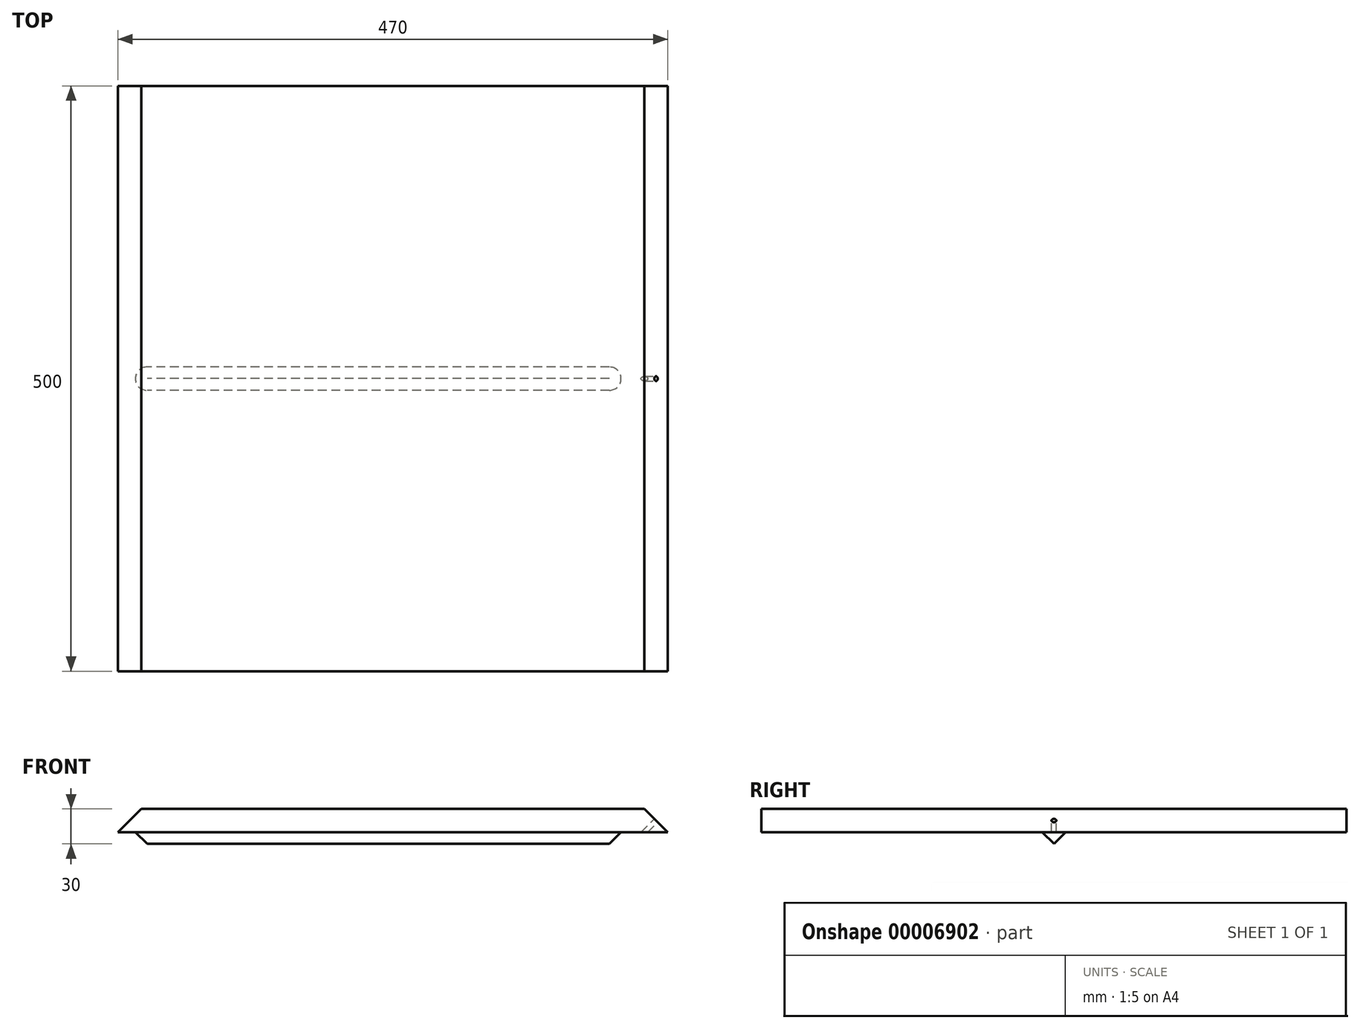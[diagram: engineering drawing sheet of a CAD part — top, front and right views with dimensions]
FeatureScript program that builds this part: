
annotation { "Feature Type Name" : "Feature", "Feature Type Description" : "" }
export const myFeature = defineFeature(function(context is Context, id is Id, definition is map)
    precondition{}
    {
        {
            var Q0;
            Q0=qCreatedBy(makeId("Top.planeOp"),FACE);
            var sketch = newSketch(context, id + "F0", { "sketchPlane" : qUnion([Q0])});
            skLineSegment(sketch, "E0.rect.bottom", {"start": v(242.5, -250) * mm, "end": v(-242.5, -250) * mm});
            skLineSegment(sketch, "E0.rect.top", {"start": v(242.5, 250) * mm, "end": v(-242.5, 250) * mm});
            skLineSegment(sketch, "E0.rect.left", {"start": v(242.5, -250) * mm, "end": v(242.5, 250) * mm});
            skLineSegment(sketch, "E0.rect.right", {"start": v(-242.5, -250) * mm, "end": v(-242.5, 250) * mm});
            skPoint(sketch, "E0.rect.middle", {"position": v(0, 0) * mm});
            skLineSegment(sketch, "E1", {"start": v(-242.5, 0) * mm, "end": v(242.5, 0) * mm, "construction": true});
            skSolve(sketch);
        }
        {
            var Q0;
            Q0=qSketchRegion(id+"F0",true);
            var Q1;
            Q1=makeQuery(id+"F0.imprint","IMPRINT",FACE,{"disambiguationData":[TD([[makeQuery(id+"F0.imprint","IMPRINT",EDGE,{"derivedFrom":sQuery(id+"F0.wireOp",EDGE,"E0.rect.bottom")}),-1.0]])]});
            extrude(context, id + "F1", {"entities" : qUnion([Q0, Q1]), "depth" : (30) * mm});
        }
        {
            var Q0;
            Q0=makeQuery(id+"F1.opExtrude","SWEPT_FACE",FACE,{"disambiguationData":[OSD([sQuery(id+"F0.wireOp",EDGE,"E0.rect.right")])]});
            var sketch = newSketch(context, id + "F2", { "sketchPlane" : qUnion([Q0])});
            skLineSegment(sketch, "E2", {"start": v(0, 0) * mm, "end": v(-10, 10) * mm});
            skLineSegment(sketch, "E3", {"start": v(0, 0) * mm, "end": v(10, 10) * mm});
            skLineSegment(sketch, "E4", {"start": v(-10, 10) * mm, "end": v(-250, 10) * mm});
            skLineSegment(sketch, "E5", {"start": v(10, 10) * mm, "end": v(250, 10) * mm});
            skSolve(sketch);
        }
        {
            var Q0;
            Q0=qSketchRegion(id+"F2",true);
            var Q1;
            {var subQ2=sQuery(id+"F2.wireOp",EDGE,"E2");Q1=makeQuery(id+"F2.imprint","IMPRINT",FACE,{"disambiguationData":[TD([[makeQuery(id+"F2.imprint","IMPRINT",EDGE,{"derivedFrom":subQ2}),1.0]])]});}
            var Q2;
            {var subQ2=sQuery(id+"F2.wireOp",EDGE,"E3");Q2=makeQuery(id+"F2.imprint","IMPRINT",FACE,{"disambiguationData":[TD([[makeQuery(id+"F2.imprint","IMPRINT",EDGE,{"derivedFrom":subQ2}),-1.0]])]});}
            extrude(context, id + "F3", {"entities" : qUnion([Q0, Q1, Q2]), "operationType" : NewBodyOperationType.REMOVE, "endBound" : BoundingType.THROUGH_ALL, "oppositeDirection" : true, "depth" : 25 * mm});
        }
        {
            var Q0;
            Q0=makeQuery(id+"F1.opExtrude","SWEPT_FACE",FACE,{"disambiguationData":[OSD([sQuery(id+"F0.wireOp",EDGE,"E0.rect.right")])]});
            var sketch = newSketch(context, id + "F4", { "sketchPlane" : qUnion([Q0])});
            skLineSegment(sketch, "E6", {"start": v(-10, 10) * mm, "end": v(10, 10) * mm});
            skSolve(sketch);
        }
        {
            var Q0;
            Q0=qSketchRegion(id+"F4",true);
            var Q1;
            Q1=makeQuery(id+"F4.imprint","IMPRINT",FACE,{"disambiguationData":[TD([[makeQuery(id+"F4.imprint","IMPRINT",EDGE,{"derivedFrom":sQuery(id+"F4.wireOp",EDGE,"E6")}),-1.0]])]});
            extrude(context, id + "F5", {"entities" : qUnion([Q0, Q1]), "operationType" : NewBodyOperationType.REMOVE, "oppositeDirection" : true, "depth" : 25 * mm});
        }
        {
            var Q0;
            Q0=makeQuery(id+"F5.boolean.opBoolean","COPY",FACE,{"derivedFrom":makeQuery(id+"F5.opExtrude","CAP_FACE",FACE,{"disambiguationData":[OSD([sQuery(id+"F2.wireOp",EDGE,"E2"),sQuery(id+"F2.wireOp",EDGE,"E3"),sQuery(id+"F4.wireOp",EDGE,"E6")])],"isStart":false})});
            var sketch = newSketch(context, id + "F6", { "sketchPlane" : qUnion([Q0])});
            skLineSegment(sketch, "E7", {"start": v(0, 0) * mm, "end": v(0, 10) * mm});
            skSolve(sketch);
        }
        {
            var Q0;
            {var subQ1=sQuery(id+"F6.wireOp",EDGE,"E7");Q0=makeQuery(id+"F6.imprint","IMPRINT",FACE,{"disambiguationData":[TD([[makeQuery(id+"F6.imprint","IMPRINT",EDGE,{"derivedFrom":subQ1}),1.0]])]});}
            var Q1;
            Q1=sQuery(id+"F6.wireOp",EDGE,"E7");
            revolve(context, id + "F7", {"operationType" : NewBodyOperationType.ADD, "entities" : qUnion([Q0]), "axis" : qUnion([Q1]), "revolveType" : RevolveType.FULL});
        }
        {
            var Q0;
            Q0=makeQuery(id+"F1.opExtrude","SWEPT_FACE",FACE,{"disambiguationData":[OSD([sQuery(id+"F0.wireOp",EDGE,"E0.rect.top")])]});
            var sketch = newSketch(context, id + "F8", { "sketchPlane" : qUnion([Q0])});
            skLineSegment(sketch, "E8", {"start": v(242.5, 10) * mm, "end": v(222.5, 30) * mm});
            skSolve(sketch);
        }
        {
            var Q0;
            Q0=qSketchRegion(id+"F8",true);
            var Q1;
            {var subQ2=sQuery(id+"F8.wireOp",EDGE,"E8");Q1=makeQuery(id+"F8.imprint","IMPRINT",FACE,{"disambiguationData":[TD([[makeQuery(id+"F8.imprint","IMPRINT",EDGE,{"derivedFrom":subQ2}),-1.0]])]});}
            extrude(context, id + "F9", {"entities" : qUnion([Q0, Q1]), "operationType" : NewBodyOperationType.REMOVE, "endBound" : BoundingType.THROUGH_ALL, "oppositeDirection" : true, "depth" : 25 * mm});
        }
        {
            var Q0;
            Q0=makeQuery(id+"F1.opExtrude","SWEPT_FACE",FACE,{"disambiguationData":[OSD([sQuery(id+"F0.wireOp",EDGE,"E0.rect.left")])]});
            extrude(context, id + "F10", {"entities" : qUnion([Q0]), "operationType" : NewBodyOperationType.REMOVE, "oppositeDirection" : true, "depth" : (15) * mm});
        }
        {
            var Q0;
            Q0=makeQuery(id+"F10.boolean.opBoolean","COPY",FACE,{"derivedFrom":makeQuery(id+"F10.opExtrude","CAP_FACE",FACE,{"disambiguationData":[OSD([sQuery(id+"F0.wireOp",EDGE,"E0.rect.left")])],"isStart":false})});
            var sketch = newSketch(context, id + "F11", { "sketchPlane" : qUnion([Q0])});
            skLineSegment(sketch, "E9", {"start": v(-10, 10) * mm, "end": v(10, 10) * mm});
            skSolve(sketch);
        }
        {
            var Q0;
            Q0=makeQuery(id+"F11.imprint","IMPRINT",FACE,{"disambiguationData":[TD([[makeQuery(id+"F11.imprint","IMPRINT",EDGE,{"derivedFrom":sQuery(id+"F11.wireOp",EDGE,"E9")}),-1.0]])]});
            extrude(context, id + "F12", {"entities" : qUnion([Q0]), "operationType" : NewBodyOperationType.REMOVE, "oppositeDirection" : true, "depth" : (50) * mm});
        }
        {
            var Q0;
            Q0=makeQuery(id+"F12.boolean.opBoolean","COPY",FACE,{"derivedFrom":makeQuery(id+"F12.opExtrude","CAP_FACE",FACE,{"disambiguationData":[OSD([sQuery(id+"F0.wireOp",EDGE,"E0.rect.left"),sQuery(id+"F2.wireOp",EDGE,"E2"),sQuery(id+"F2.wireOp",EDGE,"E3"),sQuery(id+"F11.wireOp",EDGE,"E9")])],"isStart":false})});
            var sketch = newSketch(context, id + "F13", { "sketchPlane" : qUnion([Q0])});
            skLineSegment(sketch, "E10", {"start": v(0, 0) * mm, "end": v(0, 10) * mm});
            skSolve(sketch);
        }
        {
            var Q0;
            {var subQ1=sQuery(id+"F13.wireOp",EDGE,"E10");Q0=makeQuery(id+"F13.imprint","IMPRINT",FACE,{"disambiguationData":[TD([[makeQuery(id+"F13.imprint","IMPRINT",EDGE,{"derivedFrom":subQ1}),-1.0]])]});}
            var Q1;
            Q1=sQuery(id+"F13.wireOp",EDGE,"E10");
            revolve(context, id + "F14", {"operationType" : NewBodyOperationType.ADD, "entities" : qUnion([Q0]), "axis" : qUnion([Q1]), "revolveType" : RevolveType.FULL});
        }
        {
            var Q0;
            Q0=makeQuery(id+"F1.opExtrude","SWEPT_FACE",FACE,{"disambiguationData":[OSD([sQuery(id+"F0.wireOp",EDGE,"E0.rect.top")])]});
            var sketch = newSketch(context, id + "F15", { "sketchPlane" : qUnion([Q0])});
            skLineSegment(sketch, "E11", {"start": v(-227.5, 10) * mm, "end": v(-207.5, 30) * mm});
            skSolve(sketch);
        }
        {
            var Q0;
            Q0=qSketchRegion(id+"F15",true);
            var Q1;
            {var subQ2=sQuery(id+"F15.wireOp",EDGE,"E11");Q1=makeQuery(id+"F15.imprint","IMPRINT",FACE,{"disambiguationData":[TD([[makeQuery(id+"F15.imprint","IMPRINT",EDGE,{"derivedFrom":subQ2}),1.0]])]});}
            extrude(context, id + "F16", {"entities" : qUnion([Q0, Q1]), "operationType" : NewBodyOperationType.REMOVE, "endBound" : BoundingType.THROUGH_ALL, "oppositeDirection" : true, "depth" : 25 * mm});
        }
        {
            var Q0;
            Q0=makeQuery(id+"F16.boolean.opBoolean","COPY",FACE,{"derivedFrom":makeQuery(id+"F16.opExtrude","SWEPT_FACE",FACE,{"disambiguationData":[OSD([sQuery(id+"F15.wireOp",EDGE,"E11")])]})});
            var sketch = newSketch(context, id + "F17", { "sketchPlane" : qUnion([Q0])});
            skLineSegment(sketch, "E12", {"start": v(0, -125.51) * mm, "end": v(0, -153.8) * mm, "construction": true});
            skCircle(sketch, "E13", {"center": v(0, -139.65) * mm, "radius": 2 * mm});
            skSolve(sketch);
        }
        {
            var Q0;
            Q0=qSketchRegion(id+"F17",true);
            extrude(context, id + "F18", {"entities" : qUnion([Q0]), "operationType" : NewBodyOperationType.REMOVE, "endBound" : BoundingType.THROUGH_ALL, "oppositeDirection" : true, "depth" : 25 * mm});
        }
    });
